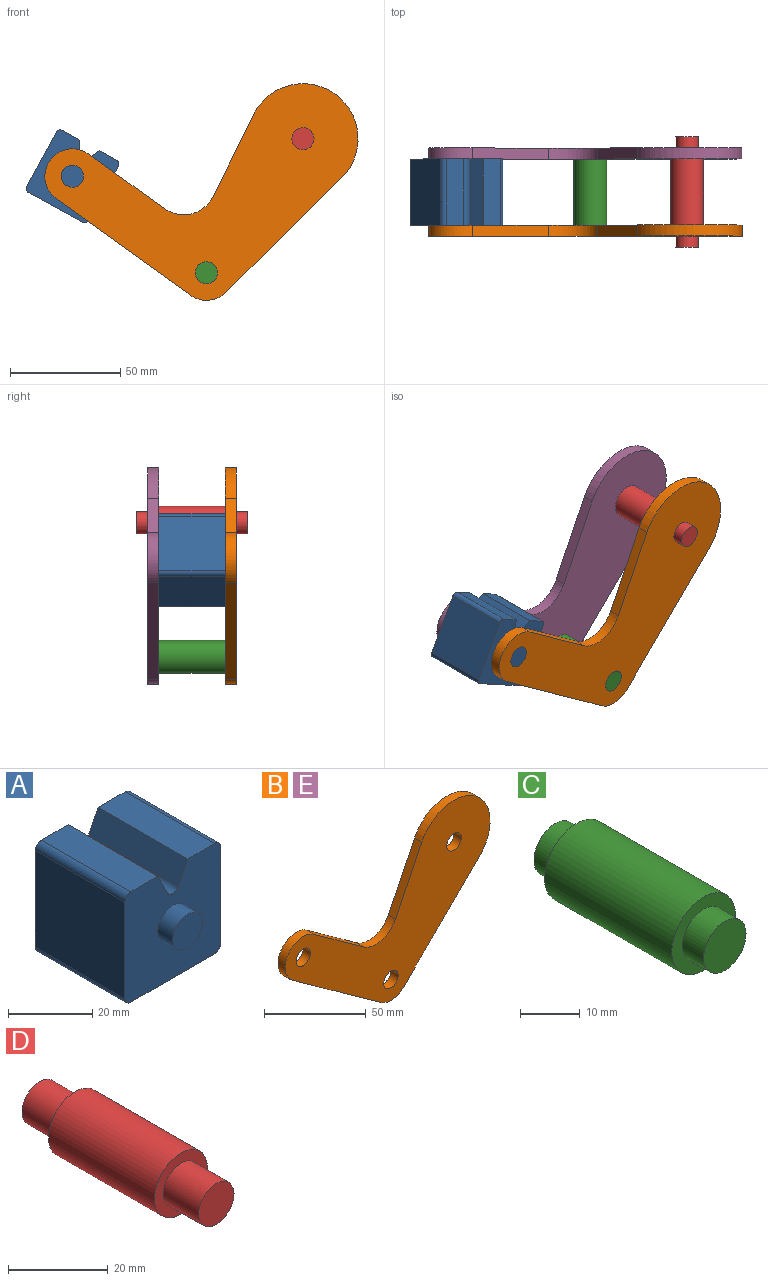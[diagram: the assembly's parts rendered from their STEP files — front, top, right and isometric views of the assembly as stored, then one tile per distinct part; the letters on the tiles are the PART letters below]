
ASSEMBLY  parts=5 mates=5
PART A: 18 faces, bbox 32.1x40x32.1 mm
  f0: plane 30x6.42mm, normal (0.89,0,0.45), area 215.4mm2, adj f4,f6,f10,f13
  f1: plane 30x6.42mm, normal (-0.89,0,0.45), area 215.4mm2, adj f2,f4,f10,f13
  f2: plane 30x9.04mm, normal (0,0,1), area 271.2mm2, adj f1,f4,f10,f14
  f3: plane 30x28.08mm, normal (1,0,0), area 842.3mm2, adj f4,f10,f14,f15
  f4: plane 32.08x32.08mm, normal (0,-1,0), area 900.6mm2, adj f0,f1,f2,f3,f5,f6,f7,f9
  f5: plane 30x28.08mm, normal (0,0,-1), area 842.3mm2, adj f4,f10,f15,f16
  f6: plane 30x9.04mm, normal (0,0,1), area 271.2mm2, adj f0,f4,f10,f17
  f7: plane 30x28.08mm, normal (-1,0,0), area 842.3mm2, adj f4,f10,f16,f17
  f8: plane 10x10mm, normal (0,-1,0), area 78.5mm2, adj f9
  f9: cylinder r=5mm len=10mm, axis (0,1,0), area 157.1mm2, adj f4,f8
  f10: plane 32.08x32.08mm, normal (0,1,0), area 900.6mm2, adj f0,f1,f2,f3,f5,f6,f7,f12
  f11: plane 10x10mm, normal (0,1,0), area 78.5mm2, adj f12
  f12: cylinder r=5mm len=10mm, axis (0,-1,0), area 157.1mm2, adj f10,f11
  f13: cylinder r=2mm len=30mm, axis (0,1,0), area 132.9mm2, adj f0,f1,f4,f10
  f14: cylinder r=2mm len=30mm, axis (0,1,0), area 94.2mm2, adj f2,f3,f4,f10
  f15: cylinder r=2mm len=30mm, axis (0,-1,0), area 94.2mm2, adj f3,f4,f5,f10
  f16: cylinder r=2mm len=30mm, axis (0,1,0), area 94.2mm2, adj f4,f5,f7,f10
  f17: cylinder r=2mm len=30mm, axis (0,-1,0), area 94.2mm2, adj f4,f6,f7,f10
PART B: 13 faces, bbox 142.2x5x98.4 mm
  f0: plane 52.61x51.97mm, normal (0.7,0,-0.71), area 369.8mm2, adj f1,f9,f11,f12
  f1: cylinder r=25mm len=47.44mm, axis (0,-1,0), area 434.6mm2, adj f0,f2,f11,f12
  f2: plane 37.17x18.26mm, normal (-0.9,0,0.44), area 207.1mm2, adj f1,f3,f11,f12
  f3: cylinder r=15mm len=22.23mm, axis (0,-1,0), area 130.4mm2, adj f2,f4,f11,f12
  f4: plane 34.46x24.81mm, normal (0.58,0,0.81), area 212.3mm2, adj f3,f5,f11,f12
  f5: cylinder r=12.5mm len=22.64mm, axis (0,-1,0), area 196.3mm2, adj f4,f6,f11,f12
  f6: plane 60.86x43.82mm, normal (-0.58,0,-0.81), area 375mm2, adj f5,f9,f11,f12
  f7: cylinder r=5mm len=10mm, axis (0,-1,0), area 157.1mm2, adj f11,f12
  f8: cylinder r=5mm len=10mm, axis (0,-1,0), area 157.1mm2, adj f11,f12
  f9: cylinder r=12.5mm len=16.09mm, axis (0,-1,0), area 87.7mm2, adj f0,f6,f11,f12
  f10: cylinder r=5mm len=10mm, axis (0,-1,0), area 157.1mm2, adj f11,f12
  f11: plane 142.19x98.36mm, normal (0,1,0), area 5739.8mm2, adj f0,f1,f2,f3,f4,f5,f6,f7
  f12: plane 142.19x98.36mm, normal (0,-1,0), area 5739.8mm2, adj f0,f1,f2,f3,f4,f5,f6,f7
PART C: 7 faces, bbox 15x40x15 mm
  f0: cylinder r=7.5mm len=30mm, axis (0,-1,0), area 1413.7mm2, adj f2,f5
  f1: cylinder r=5mm len=10mm, axis (0,-1,0), area 157.1mm2, adj f2,f3
  f2: plane 15x15mm, normal (0,-1,0), area 98.2mm2, adj f0,f1
  f3: plane 10x10mm, normal (0,-1,0), area 78.5mm2, adj f1
  f4: cylinder r=5mm len=10mm, axis (0,1,0), area 157.1mm2, adj f5,f6
  f5: plane 15x15mm, normal (0,1,0), area 98.2mm2, adj f0,f4
  f6: plane 10x10mm, normal (0,1,0), area 78.5mm2, adj f4
PART D: 7 faces, bbox 15x50x15 mm
  f0: cylinder r=7.5mm len=30mm, axis (0,-1,0), area 1413.7mm2, adj f2,f5
  f1: cylinder r=5mm len=10mm, axis (0,1,0), area 314.2mm2, adj f2,f3
  f2: plane 15x15mm, normal (0,-1,0), area 98.2mm2, adj f0,f1
  f3: plane 10x10mm, normal (0,-1,0), area 78.5mm2, adj f1
  f4: cylinder r=5mm len=10mm, axis (0,-1,0), area 314.2mm2, adj f5,f6
  f5: plane 15x15mm, normal (0,1,0), area 98.2mm2, adj f0,f4
  f6: plane 10x10mm, normal (0,1,0), area 78.5mm2, adj f4
PART E: same geometry as B
PLACE A rot(axis=(0,1,0),28.7deg) t=(-3.99,-18.13,-59.89)mm
PLACE B t=(0.72,-18.13,-7.43)mm
PLACE C t=(0.72,-18.13,-7.43)mm
PLACE D t=(0.72,-18.13,-7.43)mm fixed
PLACE E t=(0.72,16.87,-7.43)mm
MATE fastened C.f0 <-> E.f7  axis (0,-1,0) through (-43.11,16.87,-68.3)mm
MATE revolute B.f5 <-> A.f9  axis (0,-1,0) through (-103.97,-18.13,-24.47)mm
MATE revolute B.f7 <-> C.f0  axis (0,1,0) through (-43.11,-13.13,-68.3)mm
MATE revolute B.f1 <-> D.f0  axis (0,-1,0) through (0.72,-13.13,-7.43)mm
MATE fastened D.f0 <-> E.f1  axis (0,1,0) through (0.72,16.87,-7.43)mm
